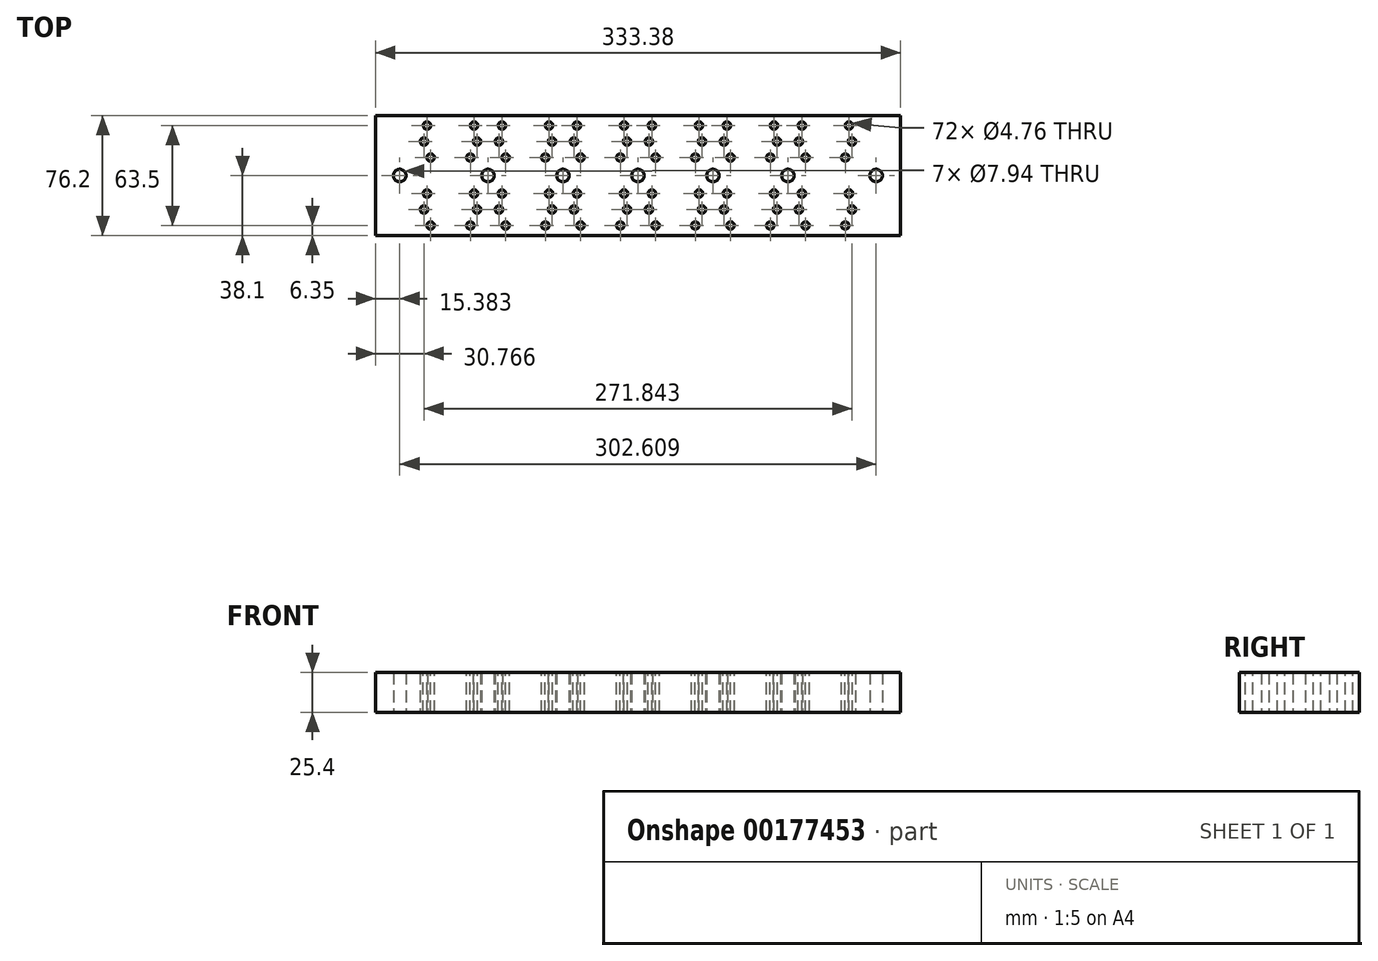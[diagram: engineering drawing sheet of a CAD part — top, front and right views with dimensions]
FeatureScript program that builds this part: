
annotation { "Feature Type Name" : "Feature", "Feature Type Description" : "" }
export const myFeature = defineFeature(function(context is Context, id is Id, definition is map)
    precondition{}
    {
        {
            var Q0;
            Q0=qCreatedBy(makeId("Top.planeOp"),FACE);
            var sketch = newSketch(context, id + "F0", { "sketchPlane" : qUnion([Q0])});
            skLineSegment(sketch, "E0.bottom", {"start": v(0, 0) * mm, "end": v(333.38, 0) * mm});
            skLineSegment(sketch, "E0.top", {"start": v(0, 76.2) * mm, "end": v(333.38, 76.2) * mm});
            skLineSegment(sketch, "E0.left", {"start": v(0, 0) * mm, "end": v(0, 76.2) * mm});
            skLineSegment(sketch, "E1", {"start": v(0, 16.51) * mm, "end": v(333.38, 16.51) * mm, "construction": true});
            skLineSegment(sketch, "E2", {"start": v(0, 59.7) * mm, "end": v(333.38, 59.7) * mm, "construction": true});
            skLineSegment(sketch, "E3", {"start": v(190.5, 101.6) * mm, "end": v(190.5, 0) * mm, "construction": true});
            skLineSegment(sketch, "E4", {"start": v(95.25, 76.2) * mm, "end": v(95.25, 0) * mm, "construction": true});
            skLineSegment(sketch, "E5", {"start": v(285.75, 76.2) * mm, "end": v(285.75, 0) * mm, "construction": true});
            skPoint(sketch, "E6", {"position": v(78.4, 59.7) * mm});
            skPoint(sketch, "E7", {"position": v(112.1, 59.7) * mm});
            skLineSegment(sketch, "E8", {"start": v(47.62, 76.2) * mm, "end": v(47.63, 0) * mm, "construction": true});
            skLineSegment(sketch, "E9", {"start": v(142.88, 76.2) * mm, "end": v(142.88, 0) * mm, "construction": true});
            skLineSegment(sketch, "E10", {"start": v(238.13, 76.2) * mm, "end": v(238.13, 0) * mm, "construction": true});
            skPoint(sketch, "E11", {"position": v(64.48, 59.7) * mm});
            skPoint(sketch, "E12", {"position": v(30.77, 59.7) * mm});
            skPoint(sketch, "E13", {"position": v(126.02, 59.7) * mm});
            skPoint(sketch, "E14", {"position": v(159.73, 59.7) * mm});
            skPoint(sketch, "E15", {"position": v(173.64, 59.7) * mm});
            skPoint(sketch, "E16", {"position": v(207.36, 59.7) * mm});
            skPoint(sketch, "E17", {"position": v(221.27, 59.7) * mm});
            skPoint(sketch, "E18", {"position": v(254.98, 59.7) * mm});
            skPoint(sketch, "E19", {"position": v(268.9, 59.7) * mm});
            skPoint(sketch, "E20", {"position": v(302.6, 59.7) * mm});
            skPoint(sketch, "E21.MirrorP", {"position": v(30.77, 16.51) * mm});
            skPoint(sketch, "E22.MirrorP", {"position": v(64.48, 16.51) * mm});
            skPoint(sketch, "E23.MirrorP", {"position": v(78.4, 16.51) * mm});
            skPoint(sketch, "E24.MirrorP", {"position": v(112.1, 16.51) * mm});
            skPoint(sketch, "E25.MirrorP", {"position": v(126.02, 16.51) * mm});
            skPoint(sketch, "E26.MirrorP", {"position": v(159.73, 16.51) * mm});
            skPoint(sketch, "E27.MirrorP", {"position": v(173.64, 16.51) * mm});
            skPoint(sketch, "E28.MirrorP", {"position": v(207.36, 16.51) * mm});
            skPoint(sketch, "E29.MirrorP", {"position": v(221.27, 16.51) * mm});
            skPoint(sketch, "E30.MirrorP", {"position": v(254.98, 16.51) * mm});
            skPoint(sketch, "E31.MirrorP", {"position": v(268.9, 16.51) * mm});
            skPoint(sketch, "E32.MirrorP", {"position": v(302.6, 16.51) * mm});
            skPoint(sketch, "E33", {"position": v(71.44, 38.1) * mm});
            skPoint(sketch, "E34", {"position": v(119.06, 38.1) * mm});
            skPoint(sketch, "E35", {"position": v(15.38, 38.1) * mm});
            skPoint(sketch, "E36", {"position": v(166.69, 38.1) * mm});
            skPoint(sketch, "E37", {"position": v(214.31, 38.1) * mm});
            skPoint(sketch, "E38", {"position": v(261.94, 38.1) * mm});
            skPoint(sketch, "E39", {"position": v(318, 38.1) * mm});
            skLineSegment(sketch, "E40", {"start": v(333.38, 0) * mm, "end": v(333.38, 76.2) * mm});
            skLineSegment(sketch, "E41", {"start": v(0, 38.1) * mm, "end": v(333.38, 38.1) * mm, "construction": true});
            skSolve(sketch);
        }
        {
            var Q0;
            Q0=makeQuery(id+"F0.imprint","IMPRINT",FACE,{"disambiguationData":[TD([[makeQuery(id+"F0.imprint","IMPRINT",EDGE,{"derivedFrom":sQuery(id+"F0.wireOp",EDGE,"E0.bottom")}),1.0]])]});
            extrude(context, id + "F1", {"entities" : qUnion([Q0]), "depth" : 25.4 * mm});
        }
        {
            var Q0;
            Q0=sQuery(id+"F0.wireOp",VERTEX,"E35");
            var Q1;
            Q1=sQuery(id+"F0.wireOp",VERTEX,"E33");
            var Q2;
            Q2=sQuery(id+"F0.wireOp",VERTEX,"E34");
            var Q3;
            Q3=sQuery(id+"F0.wireOp",VERTEX,"E36");
            var Q4;
            Q4=sQuery(id+"F0.wireOp",VERTEX,"E37");
            var Q5;
            Q5=sQuery(id+"F0.wireOp",VERTEX,"E38");
            var Q6;
            Q6=sQuery(id+"F0.wireOp",VERTEX,"E39");
            var Q7;
            Q7=sQuery(id+"F0.wireOp",VERTEX,"3b7ebb16-af60-42e1-a822-7f8d10c1b8c7");
            var Q8;
            Q8=makeQuery(id+"F1.opExtrude","SWEPT_BODY",BODY,{"disambiguationData":[OSD([sQuery(id+"F0.wireOp",EDGE,"E0.bottom"),sQuery(id+"F0.wireOp",EDGE,"E0.top"),sQuery(id+"F0.wireOp",EDGE,"E0.left"),sQuery(id+"F0.wireOp",EDGE,"E0.right")])]});
            hole(context, id + "F2", {"style" : HoleStyle.SIMPLE, "endStyle" : HoleEndStyle.BLIND, "oppositeDirection" : true, "holeDiameter" : 7.94 * mm, "holeDepth" : 50.8 * mm, "locations" : qUnion([Q0, Q1, Q2, Q3, Q4, Q5, Q6, Q7]), "scope" : qUnion([Q8])});
        }
        {
            var Q0;
            Q0=sQuery(id+"F0.wireOp",VERTEX,"E21.MirrorP");
            var Q1;
            Q1=sQuery(id+"F0.wireOp",VERTEX,"E22.MirrorP");
            var Q2;
            Q2=sQuery(id+"F0.wireOp",VERTEX,"E23.MirrorP");
            var Q3;
            Q3=sQuery(id+"F0.wireOp",VERTEX,"E24.MirrorP");
            var Q4;
            Q4=sQuery(id+"F0.wireOp",VERTEX,"E25.MirrorP");
            var Q5;
            Q5=sQuery(id+"F0.wireOp",VERTEX,"E12");
            var Q6;
            Q6=sQuery(id+"F0.wireOp",VERTEX,"E11");
            var Q7;
            Q7=sQuery(id+"F0.wireOp",VERTEX,"E6");
            var Q8;
            Q8=sQuery(id+"F0.wireOp",VERTEX,"E7");
            var Q9;
            Q9=sQuery(id+"F0.wireOp",VERTEX,"E13");
            var Q10;
            Q10=sQuery(id+"F0.wireOp",VERTEX,"E14");
            var Q11;
            Q11=sQuery(id+"F0.wireOp",VERTEX,"E15");
            var Q12;
            Q12=sQuery(id+"F0.wireOp",VERTEX,"E26.MirrorP");
            var Q13;
            Q13=sQuery(id+"F0.wireOp",VERTEX,"E27.MirrorP");
            var Q14;
            Q14=sQuery(id+"F0.wireOp",VERTEX,"E28.MirrorP");
            var Q15;
            Q15=sQuery(id+"F0.wireOp",VERTEX,"E29.MirrorP");
            var Q16;
            Q16=sQuery(id+"F0.wireOp",VERTEX,"E30.MirrorP");
            var Q17;
            Q17=sQuery(id+"F0.wireOp",VERTEX,"E31.MirrorP");
            var Q18;
            Q18=sQuery(id+"F0.wireOp",VERTEX,"E32.MirrorP");
            var Q19;
            Q19=sQuery(id+"F0.wireOp",VERTEX,"29967fc2-c22f-405e-bd7a-32a87ba475ef0.MirrorP");
            var Q20;
            Q20=sQuery(id+"F0.wireOp",VERTEX,"6229046a-b547-4e6b-b578-65ce6e8667ad0.MirrorP");
            var Q21;
            Q21=sQuery(id+"F0.wireOp",VERTEX,"E16");
            var Q22;
            Q22=sQuery(id+"F0.wireOp",VERTEX,"E17");
            var Q23;
            Q23=sQuery(id+"F0.wireOp",VERTEX,"E18");
            var Q24;
            Q24=sQuery(id+"F0.wireOp",VERTEX,"E19");
            var Q25;
            Q25=sQuery(id+"F0.wireOp",VERTEX,"E20");
            var Q26;
            Q26=sQuery(id+"F0.wireOp",VERTEX,"e32ec1e8-8135-4021-abd6-58c2541cab5f");
            var Q27;
            Q27=sQuery(id+"F0.wireOp",VERTEX,"c6d1bd10-b393-4643-b172-62ffc8735714");
            var Q28;
            Q28=makeQuery(id+"F1.opExtrude","SWEPT_BODY",BODY,{"disambiguationData":[OSD([sQuery(id+"F0.wireOp",EDGE,"E0.bottom"),sQuery(id+"F0.wireOp",EDGE,"E0.top"),sQuery(id+"F0.wireOp",EDGE,"E0.left"),sQuery(id+"F0.wireOp",EDGE,"E0.right")])]});
            hole(context, id + "F3", {"style" : HoleStyle.SIMPLE, "endStyle" : HoleEndStyle.BLIND, "oppositeDirection" : true, "holeDiameter" : 4.76 * mm, "holeDepth" : 25.4 * mm, "locations" : qUnion([Q0, Q1, Q2, Q3, Q4, Q5, Q6, Q7, Q8, Q9, Q10, Q11, Q12, Q13, Q14, Q15, Q16, Q17, Q18, Q19, Q20, Q21, Q22, Q23, Q24, Q25, Q26, Q27]), "scope" : qUnion([Q28])});
        }
        {
            var Q0;
            Q0=makeQuery(id+"F1.opExtrude","CAP_FACE",FACE,{"disambiguationData":[OSD([sQuery(id+"F0.wireOp",EDGE,"E0.bottom"),sQuery(id+"F0.wireOp",EDGE,"E0.top"),sQuery(id+"F0.wireOp",EDGE,"E0.left"),sQuery(id+"F0.wireOp",EDGE,"E40")])],"isStart":false});
            var sketch = newSketch(context, id + "F4", { "sketchPlane" : qUnion([Q0])});
            skLineSegment(sketch, "E42", {"start": v(0, 69.85) * mm, "end": v(333.38, 69.85) * mm, "construction": true});
            skLineSegment(sketch, "E43", {"start": v(0, 26.67) * mm, "end": v(333.38, 26.67) * mm, "construction": true});
            skLineSegment(sketch, "E44", {"start": v(0, 6.35) * mm, "end": v(333.38, 6.35) * mm, "construction": true});
            skLineSegment(sketch, "E45", {"start": v(0, 49.53) * mm, "end": v(333.38, 49.53) * mm, "construction": true});
            skPoint(sketch, "E46", {"position": v(32.67, 69.85) * mm});
            skPoint(sketch, "E47", {"position": v(62.58, 69.85) * mm});
            skPoint(sketch, "E48", {"position": v(80.3, 69.85) * mm});
            skPoint(sketch, "E49", {"position": v(110.2, 69.85) * mm});
            skPoint(sketch, "E50", {"position": v(127.92, 69.85) * mm});
            skPoint(sketch, "E51", {"position": v(157.83, 69.85) * mm});
            skPoint(sketch, "E52", {"position": v(175.55, 69.85) * mm});
            skPoint(sketch, "E53", {"position": v(205.45, 69.85) * mm});
            skPoint(sketch, "E54", {"position": v(223.17, 69.85) * mm});
            skPoint(sketch, "E55", {"position": v(253.08, 69.85) * mm});
            skPoint(sketch, "E56", {"position": v(270.8, 69.85) * mm});
            skPoint(sketch, "E57", {"position": v(300.7, 69.85) * mm});
            skPoint(sketch, "E58", {"position": v(35.02, 49.53) * mm});
            skPoint(sketch, "E59", {"position": v(82.65, 49.53) * mm});
            skPoint(sketch, "E60", {"position": v(107.85, 49.53) * mm});
            skPoint(sketch, "E61", {"position": v(130.27, 49.53) * mm});
            skPoint(sketch, "E62", {"position": v(60.23, 49.53) * mm});
            skPoint(sketch, "E63", {"position": v(177.9, 49.53) * mm});
            skPoint(sketch, "E64", {"position": v(203.1, 49.53) * mm});
            skPoint(sketch, "E65", {"position": v(225.52, 49.53) * mm});
            skPoint(sketch, "E66", {"position": v(250.73, 49.53) * mm});
            skPoint(sketch, "E67", {"position": v(273.15, 49.53) * mm});
            skPoint(sketch, "E68", {"position": v(298.35, 49.53) * mm});
            skLineSegment(sketch, "E69", {"start": v(0, 48.26) * mm, "end": v(333.38, 48.26) * mm, "construction": true});
            skLineSegment(sketch, "E70", {"start": v(0, 27.94) * mm, "end": v(333.38, 27.94) * mm, "construction": true});
            skPoint(sketch, "E71", {"position": v(155.48, 49.53) * mm});
            skPoint(sketch, "E72.MirrorP", {"position": v(32.67, 26.67) * mm});
            skPoint(sketch, "E73.MirrorP", {"position": v(62.58, 26.67) * mm});
            skPoint(sketch, "E74.MirrorP", {"position": v(80.3, 26.67) * mm});
            skPoint(sketch, "E75.MirrorP", {"position": v(110.2, 26.67) * mm});
            skPoint(sketch, "E76.MirrorP", {"position": v(127.92, 26.67) * mm});
            skPoint(sketch, "E77.MirrorP", {"position": v(157.83, 26.67) * mm});
            skPoint(sketch, "E78.MirrorP", {"position": v(175.55, 26.67) * mm});
            skPoint(sketch, "E79.MirrorP", {"position": v(205.45, 26.67) * mm});
            skPoint(sketch, "E80.MirrorP", {"position": v(223.17, 26.67) * mm});
            skPoint(sketch, "E81.MirrorP", {"position": v(253.08, 26.67) * mm});
            skPoint(sketch, "E82.MirrorP", {"position": v(270.8, 26.67) * mm});
            skPoint(sketch, "E83.MirrorP", {"position": v(300.7, 26.67) * mm});
            skPoint(sketch, "E84.MirrorP", {"position": v(35.02, 6.35) * mm});
            skPoint(sketch, "E85.MirrorP", {"position": v(60.23, 6.35) * mm});
            skPoint(sketch, "E86.MirrorP", {"position": v(82.65, 6.35) * mm});
            skPoint(sketch, "E87.MirrorP", {"position": v(107.85, 6.35) * mm});
            skPoint(sketch, "E88.MirrorP", {"position": v(130.27, 6.35) * mm});
            skPoint(sketch, "E89.MirrorP", {"position": v(155.48, 6.35) * mm});
            skPoint(sketch, "E90.MirrorP", {"position": v(177.9, 6.35) * mm});
            skPoint(sketch, "E91.MirrorP", {"position": v(203.1, 6.35) * mm});
            skPoint(sketch, "E92.MirrorP", {"position": v(225.52, 6.35) * mm});
            skPoint(sketch, "E93.MirrorP", {"position": v(250.73, 6.35) * mm});
            skPoint(sketch, "E94.MirrorP", {"position": v(273.15, 6.35) * mm});
            skPoint(sketch, "E95.MirrorP", {"position": v(298.35, 6.35) * mm});
            skSolve(sketch);
        }
        {
            var Q0;
            Q0=sQuery(id+"F4.wireOp",VERTEX,"E46");
            var Q1;
            Q1=sQuery(id+"F4.wireOp",VERTEX,"E58");
            var Q2;
            Q2=sQuery(id+"F4.wireOp",VERTEX,"E47");
            var Q3;
            Q3=sQuery(id+"F4.wireOp",VERTEX,"E62");
            var Q4;
            Q4=sQuery(id+"F4.wireOp",VERTEX,"E48");
            var Q5;
            Q5=sQuery(id+"F4.wireOp",VERTEX,"E59");
            var Q6;
            Q6=sQuery(id+"F4.wireOp",VERTEX,"E49");
            var Q7;
            Q7=sQuery(id+"F4.wireOp",VERTEX,"E60");
            var Q8;
            Q8=sQuery(id+"F4.wireOp",VERTEX,"E50");
            var Q9;
            Q9=sQuery(id+"F4.wireOp",VERTEX,"E61");
            var Q10;
            Q10=sQuery(id+"F4.wireOp",VERTEX,"E51");
            var Q11;
            Q11=sQuery(id+"F4.wireOp",VERTEX,"E71");
            var Q12;
            Q12=sQuery(id+"F4.wireOp",VERTEX,"E52");
            var Q13;
            Q13=sQuery(id+"F4.wireOp",VERTEX,"E63");
            var Q14;
            Q14=sQuery(id+"F4.wireOp",VERTEX,"E53");
            var Q15;
            Q15=sQuery(id+"F4.wireOp",VERTEX,"E64");
            var Q16;
            Q16=sQuery(id+"F4.wireOp",VERTEX,"E54");
            var Q17;
            Q17=sQuery(id+"F4.wireOp",VERTEX,"E65");
            var Q18;
            Q18=sQuery(id+"F4.wireOp",VERTEX,"E55");
            var Q19;
            Q19=sQuery(id+"F4.wireOp",VERTEX,"E66");
            var Q20;
            Q20=sQuery(id+"F4.wireOp",VERTEX,"E56");
            var Q21;
            Q21=sQuery(id+"F4.wireOp",VERTEX,"E67");
            var Q22;
            Q22=sQuery(id+"F4.wireOp",VERTEX,"E57");
            var Q23;
            Q23=sQuery(id+"F4.wireOp",VERTEX,"E68");
            var Q24;
            Q24=sQuery(id+"F4.wireOp",VERTEX,"E72.MirrorP");
            var Q25;
            Q25=sQuery(id+"F4.wireOp",VERTEX,"E84.MirrorP");
            var Q26;
            Q26=sQuery(id+"F4.wireOp",VERTEX,"E73.MirrorP");
            var Q27;
            Q27=sQuery(id+"F4.wireOp",VERTEX,"E85.MirrorP");
            var Q28;
            Q28=sQuery(id+"F4.wireOp",VERTEX,"E74.MirrorP");
            var Q29;
            Q29=sQuery(id+"F4.wireOp",VERTEX,"E86.MirrorP");
            var Q30;
            Q30=sQuery(id+"F4.wireOp",VERTEX,"E75.MirrorP");
            var Q31;
            Q31=sQuery(id+"F4.wireOp",VERTEX,"E87.MirrorP");
            var Q32;
            Q32=sQuery(id+"F4.wireOp",VERTEX,"E76.MirrorP");
            var Q33;
            Q33=sQuery(id+"F4.wireOp",VERTEX,"E88.MirrorP");
            var Q34;
            Q34=sQuery(id+"F4.wireOp",VERTEX,"E77.MirrorP");
            var Q35;
            Q35=sQuery(id+"F4.wireOp",VERTEX,"E89.MirrorP");
            var Q36;
            Q36=sQuery(id+"F4.wireOp",VERTEX,"E78.MirrorP");
            var Q37;
            Q37=sQuery(id+"F4.wireOp",VERTEX,"E90.MirrorP");
            var Q38;
            Q38=sQuery(id+"F4.wireOp",VERTEX,"E79.MirrorP");
            var Q39;
            Q39=sQuery(id+"F4.wireOp",VERTEX,"E91.MirrorP");
            var Q40;
            Q40=sQuery(id+"F4.wireOp",VERTEX,"E80.MirrorP");
            var Q41;
            Q41=sQuery(id+"F4.wireOp",VERTEX,"E92.MirrorP");
            var Q42;
            Q42=sQuery(id+"F4.wireOp",VERTEX,"E81.MirrorP");
            var Q43;
            Q43=sQuery(id+"F4.wireOp",VERTEX,"E93.MirrorP");
            var Q44;
            Q44=sQuery(id+"F4.wireOp",VERTEX,"E82.MirrorP");
            var Q45;
            Q45=sQuery(id+"F4.wireOp",VERTEX,"E94.MirrorP");
            var Q46;
            Q46=sQuery(id+"F4.wireOp",VERTEX,"E83.MirrorP");
            var Q47;
            Q47=sQuery(id+"F4.wireOp",VERTEX,"E95.MirrorP");
            var Q48;
            Q48=makeQuery(id+"F1.opExtrude","SWEPT_BODY",BODY,{"disambiguationData":[OSD([sQuery(id+"F0.wireOp",EDGE,"E0.bottom"),sQuery(id+"F0.wireOp",EDGE,"E0.top"),sQuery(id+"F0.wireOp",EDGE,"E0.left"),sQuery(id+"F0.wireOp",EDGE,"E40")])]});
            hole(context, id + "F5", {"style" : HoleStyle.SIMPLE, "endStyle" : HoleEndStyle.BLIND, "holeDiameter" : 4.76 * mm, "holeDepth" : 25.4 * mm, "locations" : qUnion([Q0, Q1, Q2, Q3, Q4, Q5, Q6, Q7, Q8, Q9, Q10, Q11, Q12, Q13, Q14, Q15, Q16, Q17, Q18, Q19, Q20, Q21, Q22, Q23, Q24, Q25, Q26, Q27, Q28, Q29, Q30, Q31, Q32, Q33, Q34, Q35, Q36, Q37, Q38, Q39, Q40, Q41, Q42, Q43, Q44, Q45, Q46, Q47]), "scope" : qUnion([Q48])});
        }
    });
